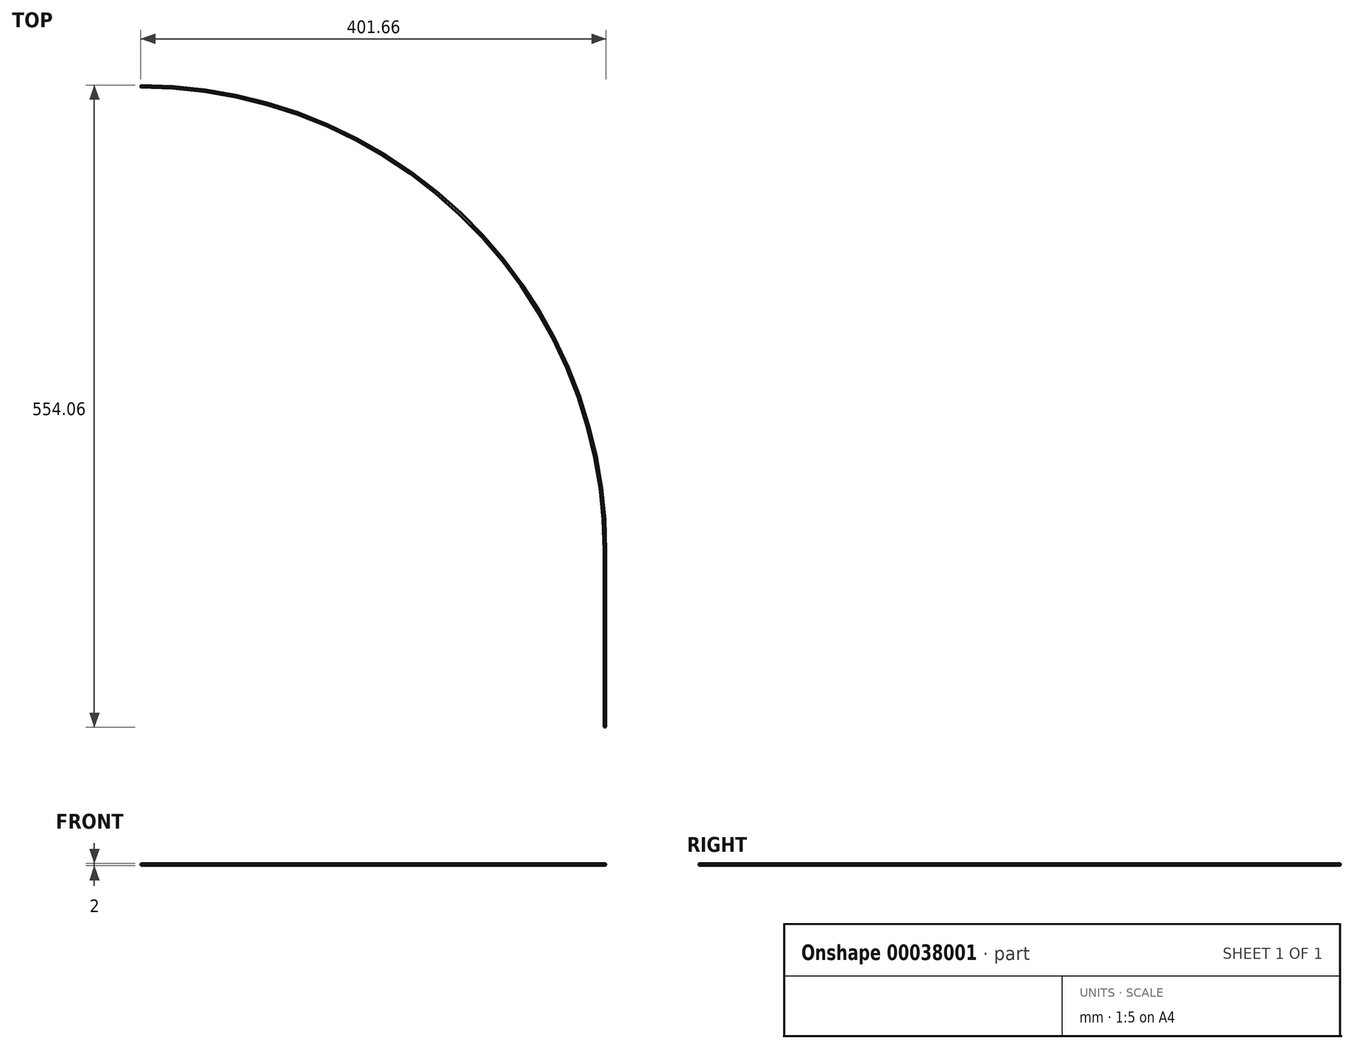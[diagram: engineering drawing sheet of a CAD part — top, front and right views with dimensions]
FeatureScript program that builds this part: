
annotation { "Feature Type Name" : "Feature", "Feature Type Description" : "" }
export const myFeature = defineFeature(function(context is Context, id is Id, definition is map)
    precondition{}
    {
        {
            var Q0;
            Q0=qCreatedBy(makeId("Top.planeOp"),FACE);
            var sketch = newSketch(context, id + "F0", { "sketchPlane" : qUnion([Q0])});
            skArc(sketch, "E0", {"start": v(400.66, -400.66) * mm, "mid": v(283.3, -117.35) * mm, "end": v(0, 0) * mm});
            skLineSegment(sketch, "E1", {"start": v(0, 0) * mm, "end": v(311.3, -524.12) * mm, "construction": true});
            skLineSegment(sketch, "E2", {"start": v(311.3, -524.12) * mm, "end": v(400.66, -400.66) * mm, "construction": true});
            skLineSegment(sketch, "E3", {"start": v(400.66, -400.66) * mm, "end": v(400.66, -553.06) * mm});
            skLineSegment(sketch, "E4", {"start": v(0, 0) * mm, "end": v(-152.4, 0) * mm, "construction": true});
            skSolve(sketch);
        }
        {
            var Q0;
            Q0=qCreatedBy(makeId("Right.planeOp"),FACE);
            var sketch = newSketch(context, id + "F1", { "sketchPlane" : qUnion([Q0])});
            skCircle(sketch, "E5", {"center": v(0, 0) * mm, "radius": 1 * mm});
            skSolve(sketch);
        }
        {
            var Q0;
            Q0 = qSketchRegion(id + "F1", true);
            var Q1;
            Q1=sQuery(id+"F0.wireOp",EDGE,"E0");
            var Q2;
            Q2=sQuery(id+"F0.wireOp",EDGE,"E3");
            sweep(context, id + "F2", {"profiles" : qUnion([Q0]), "path" : qUnion([Q1, Q2])});
        }
    });
